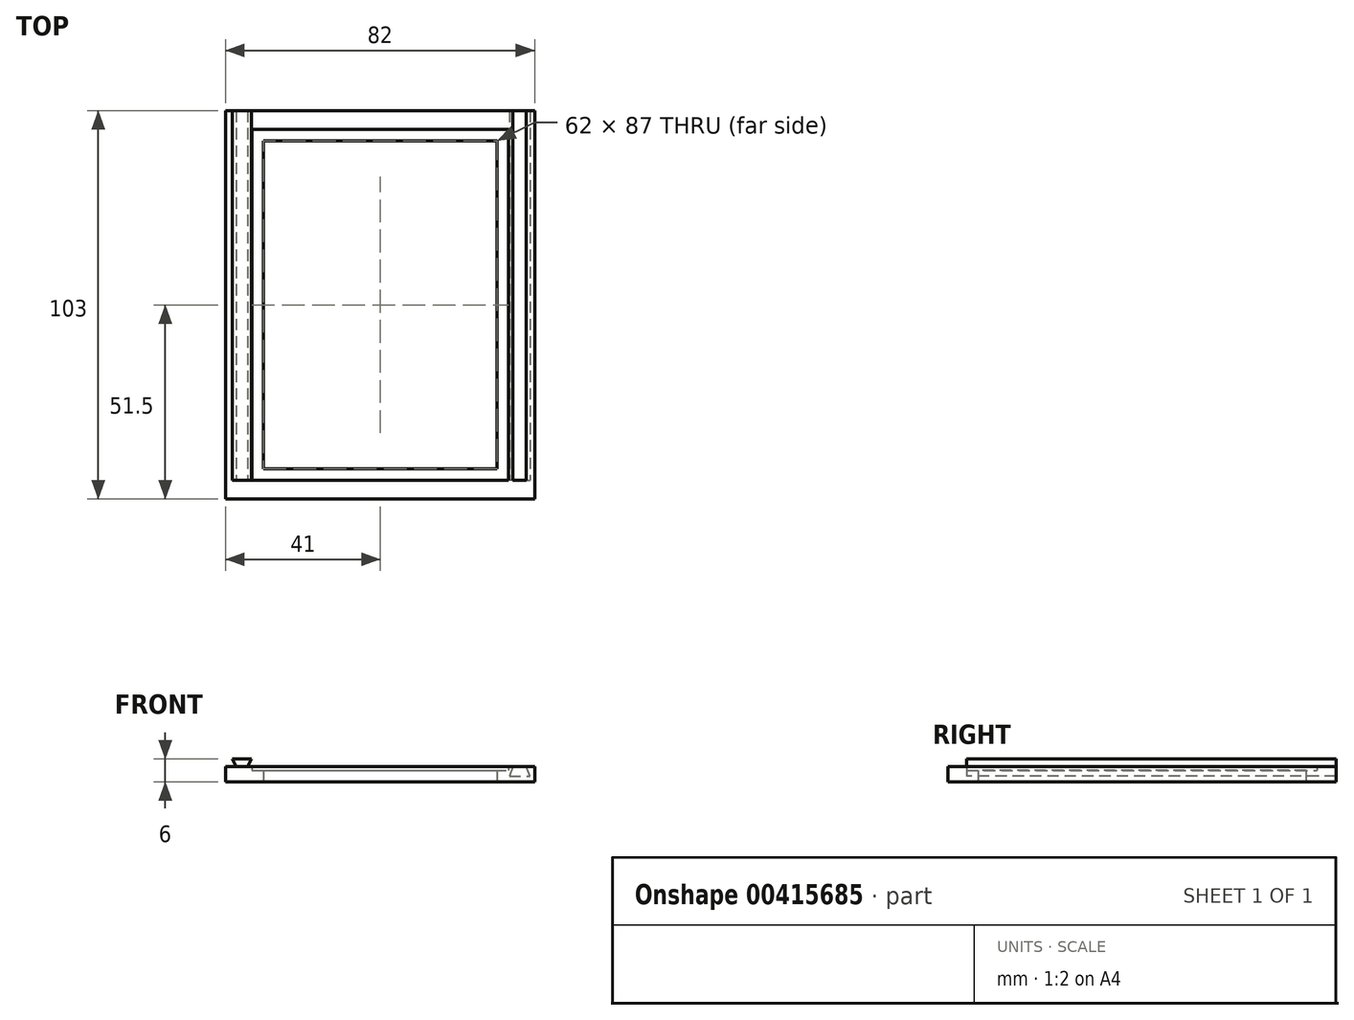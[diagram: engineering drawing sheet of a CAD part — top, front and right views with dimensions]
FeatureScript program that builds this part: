
annotation { "Feature Type Name" : "Feature", "Feature Type Description" : "" }
export const myFeature = defineFeature(function(context is Context, id is Id, definition is map)
    precondition{}
    {
        {
            var Q0;
            Q0=qCreatedBy(makeId("Top.planeOp"),FACE);
            var sketch = newSketch(context, id + "F0", { "sketchPlane" : qUnion([Q0])});
            skLineSegment(sketch, "E0.bottom", {"start": v(0, 0) * mm, "end": v(68, 0) * mm});
            skLineSegment(sketch, "E0.top", {"start": v(0, 93) * mm, "end": v(68, 93) * mm});
            skLineSegment(sketch, "E0.left", {"start": v(0, 0) * mm, "end": v(0, 93) * mm});
            skLineSegment(sketch, "E0.right", {"start": v(68, 0) * mm, "end": v(68, 93) * mm});
            skLineSegment(sketch, "E1.bottom", {"start": v(-7, 98) * mm, "end": v(75, 98) * mm});
            skLineSegment(sketch, "E1.top", {"start": v(-7, -5) * mm, "end": v(75, -5) * mm});
            skLineSegment(sketch, "E1.left", {"start": v(-7, 98) * mm, "end": v(-7, -5) * mm});
            skLineSegment(sketch, "E1.right", {"start": v(75, 98) * mm, "end": v(75, -5) * mm});
            skLineSegment(sketch, "E2.bottom", {"start": v(3, 90) * mm, "end": v(65, 90) * mm});
            skLineSegment(sketch, "E2.top", {"start": v(3, 3) * mm, "end": v(65, 3) * mm});
            skLineSegment(sketch, "E2.left", {"start": v(3, 90) * mm, "end": v(3, 3) * mm});
            skLineSegment(sketch, "E2.right", {"start": v(65, 90) * mm, "end": v(65, 3) * mm});
            skSolve(sketch);
        }
        {
            var Q0;
            Q0=makeQuery(id+"F0.imprint","IMPRINT",FACE,{"disambiguationData":[TD([[makeQuery(id+"F0.imprint","IMPRINT",EDGE,{"derivedFrom":sQuery(id+"F0.wireOp",EDGE,"E0.bottom")}),1.0]])]});
            extrude(context, id + "F1", {"entities" : qUnion([Q0]), "depth" : 3 * mm});
        }
        {
            var Q0;
            Q0 = qSketchRegion(id + "F0", true);
            extrude(context, id + "F2", {"entities" : qUnion([Q0]), "operationType" : NewBodyOperationType.ADD, "depth" : 4 * mm});
        }
        {
            var Q0;
            Q0=qCreatedBy(makeId("Front.planeOp"),FACE);
            var sketch = newSketch(context, id + "F3", { "sketchPlane" : qUnion([Q0])});
            skLineSegment(sketch, "E3", {"start": v(-4.17, 4) * mm, "end": v(-1.17, 4) * mm});
            skLineSegment(sketch, "E4", {"start": v(-1.17, 4) * mm, "end": v(-0.17, 6) * mm});
            skLineSegment(sketch, "E5", {"start": v(-0.17, 6) * mm, "end": v(-5.17, 6) * mm});
            skLineSegment(sketch, "E6", {"start": v(-5.17, 6) * mm, "end": v(-4.17, 4) * mm});
            skLineSegment(sketch, "E7", {"start": v(72.75, 4) * mm, "end": v(69.25, 4) * mm});
            skLineSegment(sketch, "E8", {"start": v(69.25, 4) * mm, "end": v(68.25, 1.5) * mm});
            skLineSegment(sketch, "E9", {"start": v(68.25, 1.5) * mm, "end": v(73.75, 1.5) * mm});
            skLineSegment(sketch, "E10", {"start": v(73.75, 1.5) * mm, "end": v(72.75, 4) * mm});
            skSolve(sketch);
        }
        {
            var Q0;
            Q0=makeQuery(id+"F3.imprint","IMPRINT",FACE,{"disambiguationData":[TD([[makeQuery(id+"F3.imprint","IMPRINT",EDGE,{"derivedFrom":sQuery(id+"F3.wireOp",EDGE,"E3")}),1.0]])]});
            extrude(context, id + "F4", {"entities" : qUnion([Q0]), "operationType" : NewBodyOperationType.ADD, "oppositeDirection" : true, "depth" : 98 * mm});
        }
        {
            var Q0;
            Q0=qCreatedBy(makeId("Front.planeOp"),FACE);
            var sketch = newSketch(context, id + "F5", { "sketchPlane" : qUnion([Q0])});
            skLineSegment(sketch, "E11", {"start": v(69.25, 4) * mm, "end": v(68.25, 1.5) * mm});
            skLineSegment(sketch, "E12", {"start": v(68.25, 1.5) * mm, "end": v(73.75, 1.5) * mm});
            skLineSegment(sketch, "E13", {"start": v(73.75, 1.5) * mm, "end": v(72.75, 4) * mm});
            skLineSegment(sketch, "E14", {"start": v(72.75, 4) * mm, "end": v(69.25, 4) * mm});
            skSolve(sketch);
        }
        {
            var Q0;
            Q0 = qSketchRegion(id + "F5", true);
            extrude(context, id + "F6", {"entities" : qUnion([Q0]), "operationType" : NewBodyOperationType.REMOVE, "oppositeDirection" : true, "depth" : 98 * mm});
        }
    });
